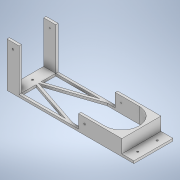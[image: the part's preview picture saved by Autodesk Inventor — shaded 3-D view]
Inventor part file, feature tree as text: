
AUTODESK INVENTOR PART (.ipt)
format: ipt  version: 2020 (Build 240168000, 168)  size: 237,056 bytes
history: native  units: mm
features: sketch x5, other x3, extrude x3, hole x2, mirror x1
ambient origin geometry x8: Origin, YZ Plane, XZ Plane, XY Plane, X Axis, Y Axis, Z Axis, Center Point
bodies: Body1 (feature_tree)
feature tree (14):
  other  "Твердое тело1"
  extrude  "Выдавливание1"  Depth=105.5mm
  extrude  "Выдавливание2"  Depth=10.0mm
  extrude  "Выдавливание3"  Depth=10.0mm
  hole  "Отверстие1"  [1 undecoded]
  mirror  "Зеркальное отражение1"
  hole  "Отверстие2"  [1 undecoded]
  sketch  "Эскиз1"
  sketch  "Эскиз2"
  sketch  "Эскиз3"
  sketch  "Эскиз4"
  sketch  "Эскиз5"
  other  "Проецирование ребер1"
  other  "Проецирование ребер2"
note: 2 required parameter values undecoded (feature->parameter linkage not recoverable at this tier; creation-order binding heuristic only, values carry confidence <= 0.55)
